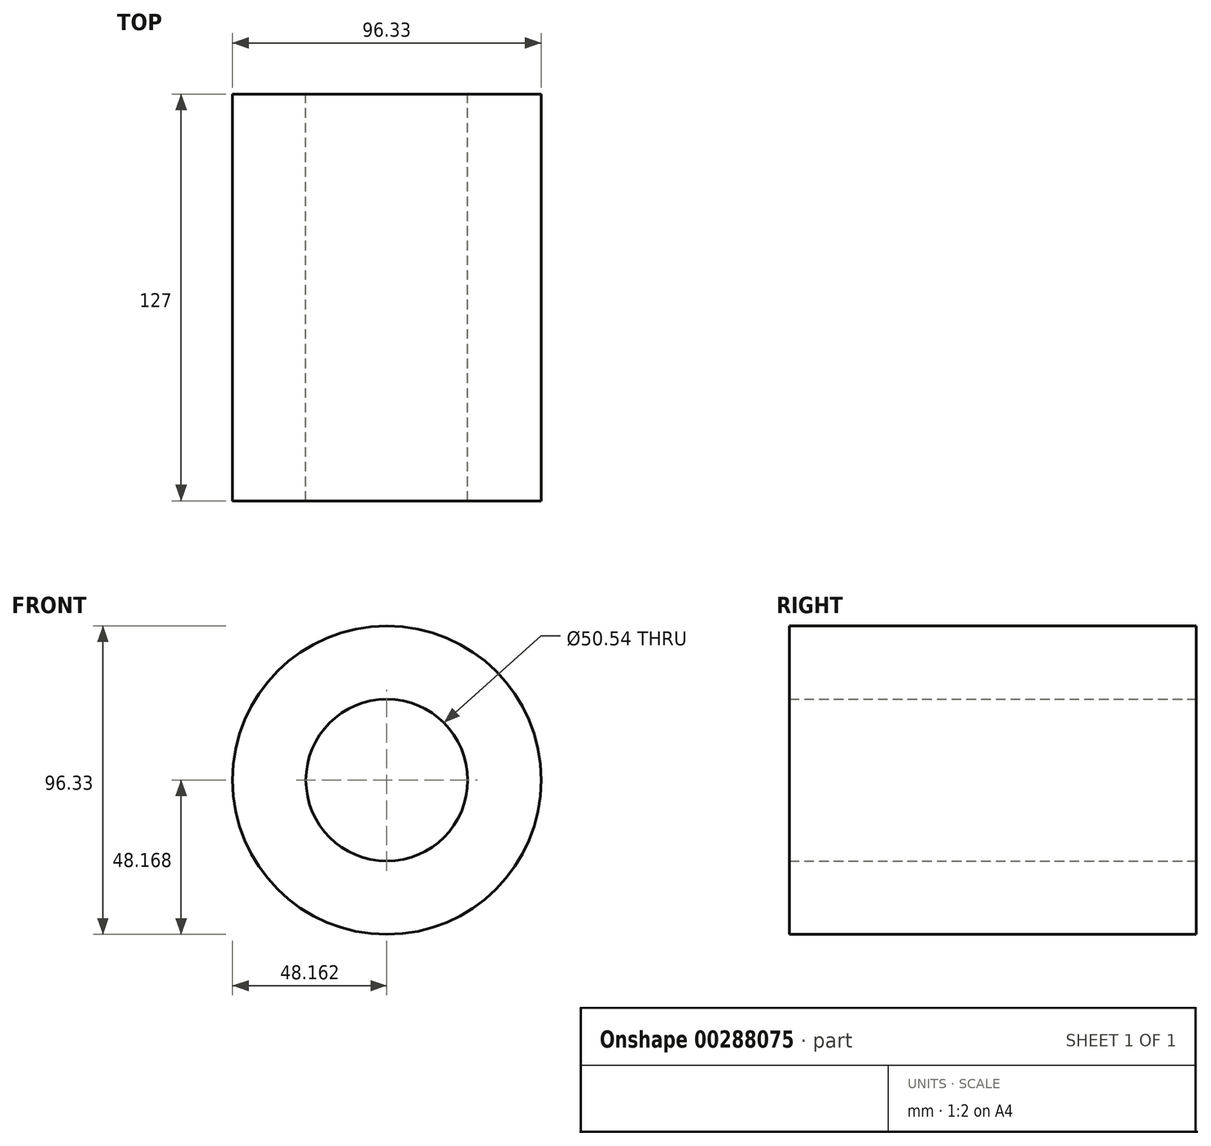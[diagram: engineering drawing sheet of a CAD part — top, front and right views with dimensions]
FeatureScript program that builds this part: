
annotation { "Feature Type Name" : "Feature", "Feature Type Description" : "" }
export const myFeature = defineFeature(function(context is Context, id is Id, definition is map)
    precondition{}
    {
        {
            var Q0;
            Q0=qCreatedBy(makeId("Front.planeOp"),FACE);
            var sketch = newSketch(context, id + "F0", { "sketchPlane" : qUnion([Q0])});
            skCircle(sketch, "E0", {"center": v(2.3, -3.74) * mm, "radius": 8.29 * mm});
            skCircle(sketch, "E1", {"center": v(2.3, -3.74) * mm, "radius": 25.27 * mm});
            skCircle(sketch, "E2", {"center": v(2.3, -3.74) * mm, "radius": 48.17 * mm});
            skSolve(sketch);
        }
        {
            var Q0;
            Q0=makeQuery(id+"F0.imprint","IMPRINT",FACE,{"disambiguationData":[TD([[makeQuery(id+"F0.imprint","IMPRINT",EDGE,{"derivedFrom":sQuery(id+"F0.wireOp",EDGE,"E1")}),-1.0]])]});
            extrude(context, id + "F1", {"entities" : qUnion([Q0]), "depth" : 127 * mm});
        }
    });
